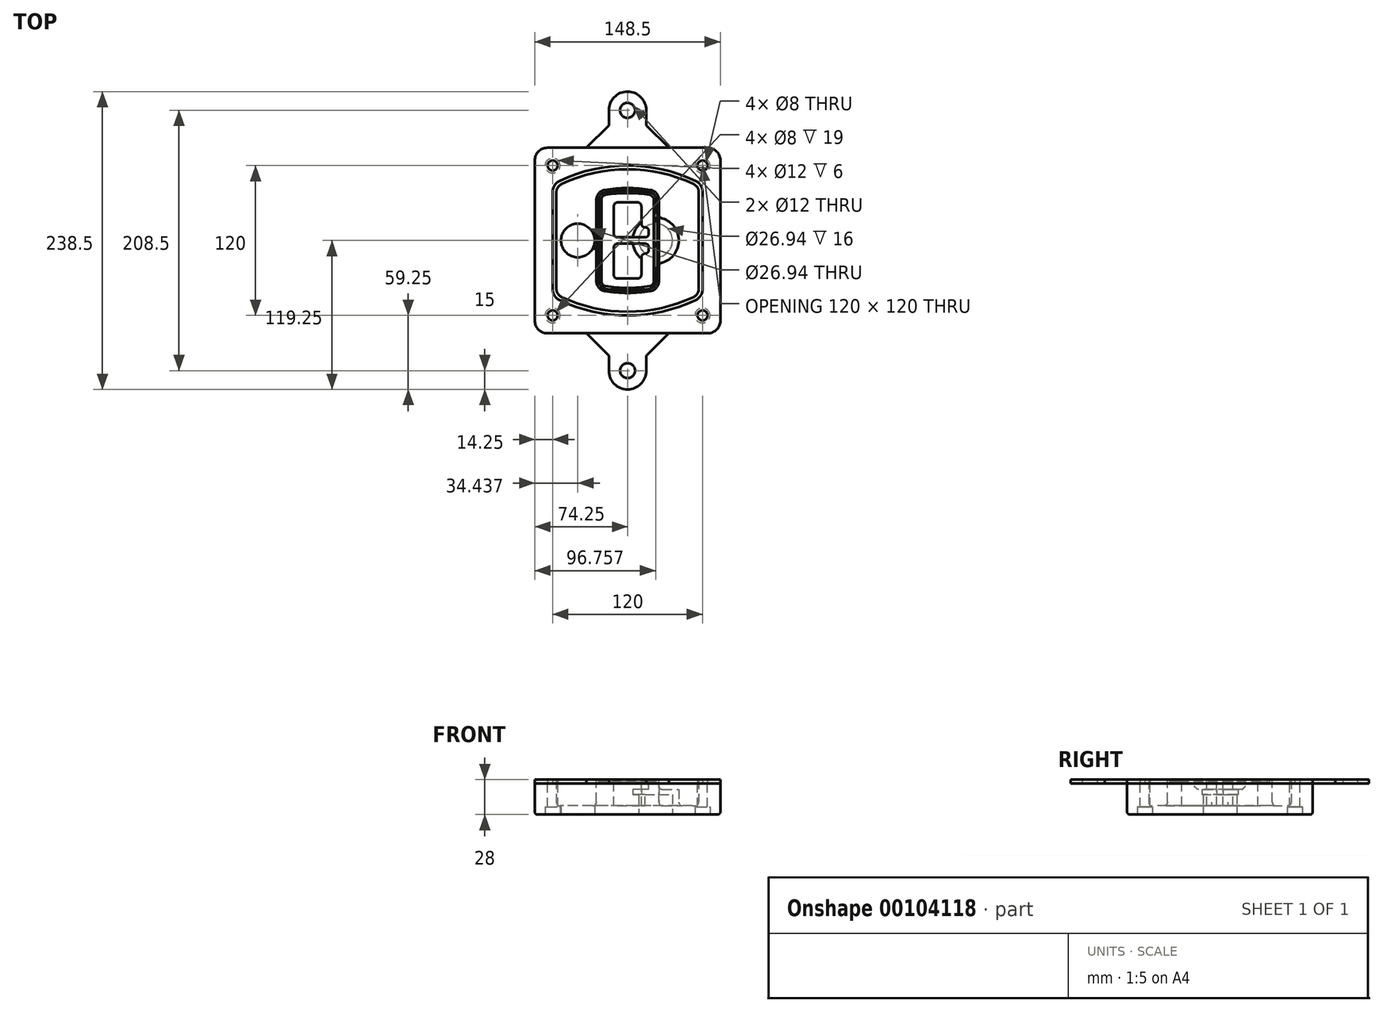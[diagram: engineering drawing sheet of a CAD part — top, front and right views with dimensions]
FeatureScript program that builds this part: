
annotation { "Feature Type Name" : "Feature", "Feature Type Description" : "" }
export const myFeature = defineFeature(function(context is Context, id is Id, definition is map)
    precondition{}
    {
        {
            var Q0;
            Q0=qCreatedBy(makeId("Top.planeOp"),FACE);
            var sketch = newSketch(context, id + "F0", { "sketchPlane" : qUnion([Q0])});
            skPoint(sketch, "E0.rect.middle", {"position": v(0, 0) * mm});
            skLineSegment(sketch, "E1.bottom", {"start": v(-64.25, -74.25) * mm, "end": v(64.25, -74.25) * mm});
            skLineSegment(sketch, "E1.top", {"start": v(-64.25, 74.25) * mm, "end": v(64.25, 74.25) * mm});
            skLineSegment(sketch, "E1.left", {"start": v(-74.25, -64.25) * mm, "end": v(-74.25, 64.25) * mm});
            skLineSegment(sketch, "E1.right", {"start": v(74.25, -64.25) * mm, "end": v(74.25, 64.25) * mm});
            skLineSegment(sketch, "E2", {"start": v(-74.25, 74.25) * mm, "end": v(74.25, -74.25) * mm, "construction": true});
            skLineSegment(sketch, "E3", {"start": v(74.25, 74.25) * mm, "end": v(-74.25, -74.25) * mm, "construction": true});
            skCircle(sketch, "E4", {"center": v(-60, 60) * mm, "radius": 4 * mm});
            skCircle(sketch, "E5", {"center": v(60, 60) * mm, "radius": 4 * mm});
            skCircle(sketch, "E6", {"center": v(60, -60) * mm, "radius": 4 * mm});
            skCircle(sketch, "E7", {"center": v(-60, -60) * mm, "radius": 4 * mm});
            skLineSegment(sketch, "E8", {"start": v(-60, 60) * mm, "end": v(60, 60) * mm, "construction": true});
            skLineSegment(sketch, "E9", {"start": v(60, 60) * mm, "end": v(60, -60) * mm, "construction": true});
            skLineSegment(sketch, "E10", {"start": v(60, -60) * mm, "end": v(-60, -60) * mm, "construction": true});
            skLineSegment(sketch, "E11", {"start": v(-60, -60) * mm, "end": v(-60, 60) * mm, "construction": true});
            skLineSegment(sketch, "E12", {"start": v(-60, 38.83) * mm, "end": v(-60, -38.83) * mm});
            skLineSegment(sketch, "E13", {"start": v(60, 38.83) * mm, "end": v(60, -38.83) * mm});
            skArc(sketch, "E14", {"start": v(54.26, 47.88) * mm, "mid": v(0, 60) * mm, "end": v(-54.26, 47.88) * mm});
            skArc(sketch, "E15", {"start": v(-54.26, -47.88) * mm, "mid": v(0, -60) * mm, "end": v(54.26, -47.88) * mm});
            skLineSegment(sketch, "E16", {"start": v(-60, 0) * mm, "end": v(60, 0) * mm, "construction": true});
            skPoint(sketch, "E17.visualSharp", {"position": v(-60, -45) * mm});
            skArc(sketch, "E17.filletArc", {"start": v(-60, -38.83) * mm, "mid": v(-58.44, -44.2) * mm, "end": v(-54.26, -47.88) * mm});
            skPoint(sketch, "E18.visualSharp", {"position": v(-60, 45) * mm});
            skArc(sketch, "E18.filletArc", {"start": v(-54.26, 47.88) * mm, "mid": v(-58.44, 44.2) * mm, "end": v(-60, 38.83) * mm});
            skPoint(sketch, "E19.visualSharp", {"position": v(60, 45) * mm});
            skArc(sketch, "E19.filletArc", {"start": v(60, 38.83) * mm, "mid": v(58.44, 44.2) * mm, "end": v(54.26, 47.88) * mm});
            skPoint(sketch, "E20.visualSharp", {"position": v(60, -45) * mm});
            skArc(sketch, "E20.filletArc", {"start": v(54.26, -47.88) * mm, "mid": v(58.44, -44.2) * mm, "end": v(60, -38.83) * mm});
            skPoint(sketch, "E21.visualSharp", {"position": v(-74.25, 74.25) * mm});
            skArc(sketch, "E21.filletArc", {"start": v(-64.25, 74.25) * mm, "mid": v(-71.32, 71.32) * mm, "end": v(-74.25, 64.25) * mm});
            skPoint(sketch, "E22.visualSharp", {"position": v(74.25, 74.25) * mm});
            skArc(sketch, "E22.filletArc", {"start": v(74.25, 64.25) * mm, "mid": v(71.32, 71.32) * mm, "end": v(64.25, 74.25) * mm});
            skPoint(sketch, "E23.visualSharp", {"position": v(74.25, -74.25) * mm});
            skArc(sketch, "E23.filletArc", {"start": v(64.25, -74.25) * mm, "mid": v(71.32, -71.32) * mm, "end": v(74.25, -64.25) * mm});
            skPoint(sketch, "E24.visualSharp", {"position": v(-74.25, -74.25) * mm});
            skArc(sketch, "E24.filletArc", {"start": v(-74.25, -64.25) * mm, "mid": v(-71.32, -71.32) * mm, "end": v(-64.25, -74.25) * mm});
            skArc(sketch, "E25.0", {"start": v(57, 38.83) * mm, "mid": v(55.9, 42.58) * mm, "end": v(52.98, 45.17) * mm});
            skLineSegment(sketch, "E25.1", {"start": v(57, 38.83) * mm, "end": v(57, -38.83) * mm});
            skArc(sketch, "E25.2", {"start": v(52.98, -45.17) * mm, "mid": v(55.9, -42.58) * mm, "end": v(57, -38.83) * mm});
            skArc(sketch, "E25.3", {"start": v(-52.98, -45.17) * mm, "mid": v(0, -57) * mm, "end": v(52.98, -45.17) * mm});
            skArc(sketch, "E25.4", {"start": v(-57, -38.83) * mm, "mid": v(-55.9, -42.58) * mm, "end": v(-52.98, -45.17) * mm});
            skArc(sketch, "E25.5", {"start": v(52.98, 45.17) * mm, "mid": v(0, 57) * mm, "end": v(-52.98, 45.17) * mm});
            skLineSegment(sketch, "E25.6", {"start": v(-57, 38.83) * mm, "end": v(-57, -38.83) * mm});
            skArc(sketch, "E25.7", {"start": v(-52.98, 45.17) * mm, "mid": v(-55.9, 42.58) * mm, "end": v(-57, 38.83) * mm});
            skArc(sketch, "E26.0", {"start": v(-55.96, 51.5) * mm, "mid": v(-61.82, 46.33) * mm, "end": v(-64, 38.83) * mm});
            skArc(sketch, "E26.1", {"start": v(55.96, 51.5) * mm, "mid": v(0, 64) * mm, "end": v(-55.96, 51.5) * mm});
            skArc(sketch, "E26.2", {"start": v(64, 38.83) * mm, "mid": v(61.82, 46.33) * mm, "end": v(55.96, 51.5) * mm});
            skLineSegment(sketch, "E26.3", {"start": v(64, 38.83) * mm, "end": v(64, -38.83) * mm});
            skArc(sketch, "E26.4", {"start": v(55.96, -51.5) * mm, "mid": v(61.82, -46.33) * mm, "end": v(64, -38.83) * mm});
            skLineSegment(sketch, "E26.5", {"start": v(-64, 38.83) * mm, "end": v(-64, -38.83) * mm});
            skArc(sketch, "E26.6", {"start": v(-55.96, -51.5) * mm, "mid": v(0, -64) * mm, "end": v(55.96, -51.5) * mm});
            skArc(sketch, "E26.7", {"start": v(-64, -38.83) * mm, "mid": v(-61.82, -46.33) * mm, "end": v(-55.96, -51.5) * mm});
            skSolve(sketch);
        }
        {
            var Q0;
            Q0=makeQuery(id+"F0.imprint","IMPRINT",FACE,{"disambiguationData":[TD([[makeQuery(id+"F0.imprint","IMPRINT",EDGE,{"derivedFrom":sQuery(id+"F0.wireOp",EDGE,"E1.bottom")}),1.0]])]});
            var Q1;
            Q1=makeQuery(id+"F0.imprint","IMPRINT",FACE,{"disambiguationData":[TD([[makeQuery(id+"F0.imprint","IMPRINT",EDGE,{"derivedFrom":sQuery(id+"F0.wireOp",EDGE,"E12")}),1.0]])]});
            var Q2;
            Q2=makeQuery(id+"F0.imprint","IMPRINT",FACE,{"disambiguationData":[TD([[makeQuery(id+"F0.imprint","IMPRINT",EDGE,{"derivedFrom":sQuery(id+"F0.wireOp",EDGE,"E25.0")}),1.0]])]});
            var Q3;
            Q3=makeQuery(id+"F0.imprint","IMPRINT",FACE,{"disambiguationData":[TD([[makeQuery(id+"F0.imprint","IMPRINT",EDGE,{"derivedFrom":sQuery(id+"F0.wireOp",EDGE,"E12")}),-1.0]])]});
            extrude(context, id + "F1", {"entities" : qUnion([Q0, Q1, Q2, Q3]), "oppositeDirection" : true, "depth" : 25 * mm});
        }
        {
            var Q0;
            Q0=makeQuery(id+"F0.imprint","IMPRINT",FACE,{"disambiguationData":[TD([[makeQuery(id+"F0.imprint","IMPRINT",EDGE,{"derivedFrom":sQuery(id+"F0.wireOp",EDGE,"E12")}),1.0]])]});
            extrude(context, id + "F2", {"entities" : qUnion([Q0]), "operationType" : NewBodyOperationType.ADD, "depth" : 3 * mm});
        }
        {
            var Q0;
            Q0=makeQuery(id+"F0.imprint","IMPRINT",FACE,{"disambiguationData":[TD([[makeQuery(id+"F0.imprint","IMPRINT",EDGE,{"derivedFrom":sQuery(id+"F0.wireOp",EDGE,"E25.0")}),1.0]])]});
            extrude(context, id + "F3", {"entities" : qUnion([Q0]), "operationType" : NewBodyOperationType.REMOVE, "oppositeDirection" : true, "depth" : 18 * mm});
        }
        {
            var Q0;
            Q0=makeQuery(id+"F2.opExtrude","CAP_FACE",FACE,{"disambiguationData":[OSD([sQuery(id+"F0.wireOp",EDGE,"E12"),sQuery(id+"F0.wireOp",EDGE,"E13"),sQuery(id+"F0.wireOp",EDGE,"E14"),sQuery(id+"F0.wireOp",EDGE,"E15"),sQuery(id+"F0.wireOp",EDGE,"E17.filletArc"),sQuery(id+"F0.wireOp",EDGE,"E18.filletArc"),sQuery(id+"F0.wireOp",EDGE,"E19.filletArc"),sQuery(id+"F0.wireOp",EDGE,"E20.filletArc"),sQuery(id+"F0.wireOp",EDGE,"E25.0"),sQuery(id+"F0.wireOp",EDGE,"E25.1"),sQuery(id+"F0.wireOp",EDGE,"E25.2"),sQuery(id+"F0.wireOp",EDGE,"E25.3"),sQuery(id+"F0.wireOp",EDGE,"E25.4"),sQuery(id+"F0.wireOp",EDGE,"E25.5"),sQuery(id+"F0.wireOp",EDGE,"E25.6"),sQuery(id+"F0.wireOp",EDGE,"E25.7")])],"isStart":false});
            var sketch = newSketch(context, id + "F4", { "sketchPlane" : qUnion([Q0])});
            skArc(sketch, "E27.0", {"start": v(-18.34, -40.45) * mm, "mid": v(0, -42) * mm, "end": v(18.34, -40.45) * mm});
            skArc(sketch, "E28.0", {"start": v(18.34, 40.45) * mm, "mid": v(0, 42) * mm, "end": v(-18.34, 40.45) * mm});
            skLineSegment(sketch, "E29", {"start": v(-25, 32.57) * mm, "end": v(-25, -32.57) * mm});
            skLineSegment(sketch, "E30", {"start": v(25, 32.57) * mm, "end": v(25, -32.57) * mm});
            skLineSegment(sketch, "E31", {"start": v(-25, 39.1) * mm, "end": v(25, 39.1) * mm, "construction": true});
            skLineSegment(sketch, "E32", {"start": v(-25, -39.1) * mm, "end": v(25, -39.1) * mm, "construction": true});
            skPoint(sketch, "E33.visualSharp", {"position": v(-25, 39.1) * mm});
            skArc(sketch, "E33.filletArc", {"start": v(-18.34, 40.45) * mm, "mid": v(-23.11, 37.73) * mm, "end": v(-25, 32.57) * mm});
            skPoint(sketch, "E34.visualSharp", {"position": v(25, 39.1) * mm});
            skArc(sketch, "E34.filletArc", {"start": v(25, 32.57) * mm, "mid": v(23.11, 37.73) * mm, "end": v(18.34, 40.45) * mm});
            skPoint(sketch, "E35.visualSharp", {"position": v(25, -39.1) * mm});
            skArc(sketch, "E35.filletArc", {"start": v(18.34, -40.45) * mm, "mid": v(23.11, -37.73) * mm, "end": v(25, -32.57) * mm});
            skPoint(sketch, "E36.visualSharp", {"position": v(-25, -39.1) * mm});
            skArc(sketch, "E36.filletArc", {"start": v(-25, -32.57) * mm, "mid": v(-23.11, -37.73) * mm, "end": v(-18.34, -40.45) * mm});
            skArc(sketch, "E37.0", {"start": v(52.98, 45.17) * mm, "mid": v(0, 57) * mm, "end": v(-52.98, 45.17) * mm});
            skArc(sketch, "E37.1", {"start": v(-52.98, 45.17) * mm, "mid": v(-55.9, 42.58) * mm, "end": v(-57, 38.83) * mm});
            skLineSegment(sketch, "E37.2", {"start": v(-57, 38.83) * mm, "end": v(-57, -38.83) * mm});
            skArc(sketch, "E37.3", {"start": v(-57, -38.83) * mm, "mid": v(-55.9, -42.58) * mm, "end": v(-52.98, -45.17) * mm});
            skArc(sketch, "E37.4", {"start": v(-52.98, -45.17) * mm, "mid": v(0, -57) * mm, "end": v(52.98, -45.17) * mm});
            skArc(sketch, "E37.5", {"start": v(52.98, -45.17) * mm, "mid": v(55.9, -42.58) * mm, "end": v(57, -38.83) * mm});
            skLineSegment(sketch, "E37.6", {"start": v(57, 38.83) * mm, "end": v(57, -38.83) * mm});
            skArc(sketch, "E37.7", {"start": v(57, 38.83) * mm, "mid": v(55.9, 42.58) * mm, "end": v(52.98, 45.17) * mm});
            skLineSegment(sketch, "E38.0", {"start": v(23, 32.57) * mm, "end": v(23, -32.57) * mm});
            skArc(sketch, "E38.1", {"start": v(18, -38.48) * mm, "mid": v(21.58, -36.44) * mm, "end": v(23, -32.57) * mm});
            skArc(sketch, "E38.2", {"start": v(-18, -38.48) * mm, "mid": v(0, -40) * mm, "end": v(18, -38.48) * mm});
            skArc(sketch, "E38.3", {"start": v(-23, -32.57) * mm, "mid": v(-21.58, -36.44) * mm, "end": v(-18, -38.48) * mm});
            skLineSegment(sketch, "E38.4", {"start": v(-23, 32.57) * mm, "end": v(-23, -32.57) * mm});
            skArc(sketch, "E38.5", {"start": v(23, 32.57) * mm, "mid": v(21.58, 36.44) * mm, "end": v(18, 38.48) * mm});
            skArc(sketch, "E38.6", {"start": v(-18, 38.48) * mm, "mid": v(-21.58, 36.44) * mm, "end": v(-23, 32.57) * mm});
            skArc(sketch, "E38.7", {"start": v(18, 38.48) * mm, "mid": v(0, 40) * mm, "end": v(-18, 38.48) * mm});
            skArc(sketch, "E39.0", {"start": v(21, 32.57) * mm, "mid": v(20.06, 35.15) * mm, "end": v(17.67, 36.5) * mm});
            skLineSegment(sketch, "E39.1", {"start": v(21, 32.57) * mm, "end": v(21, -32.57) * mm});
            skArc(sketch, "E39.2", {"start": v(17.67, -36.5) * mm, "mid": v(20.06, -35.15) * mm, "end": v(21, -32.57) * mm});
            skArc(sketch, "E39.3", {"start": v(-17.67, -36.5) * mm, "mid": v(0, -38) * mm, "end": v(17.67, -36.5) * mm});
            skArc(sketch, "E39.4", {"start": v(-21, -32.57) * mm, "mid": v(-20.06, -35.15) * mm, "end": v(-17.67, -36.5) * mm});
            skArc(sketch, "E39.5", {"start": v(17.67, 36.5) * mm, "mid": v(0, 38) * mm, "end": v(-17.67, 36.5) * mm});
            skLineSegment(sketch, "E39.6", {"start": v(-21, 32.57) * mm, "end": v(-21, -32.57) * mm});
            skArc(sketch, "E39.7", {"start": v(-17.67, 36.5) * mm, "mid": v(-20.06, 35.15) * mm, "end": v(-21, 32.57) * mm});
            skLineSegment(sketch, "E40", {"start": v(-25, 0) * mm, "end": v(25, 0) * mm, "construction": true});
            skLineSegment(sketch, "E41", {"start": v(-11, 5.5) * mm, "end": v(-11, 27.5) * mm});
            skLineSegment(sketch, "E42", {"start": v(-8, 30.5) * mm, "end": v(8, 30.5) * mm});
            skLineSegment(sketch, "E43", {"start": v(11, 27.5) * mm, "end": v(11, 13.5) * mm});
            skLineSegment(sketch, "E44", {"start": v(14, 10.5) * mm, "end": v(14, 10.5) * mm});
            skLineSegment(sketch, "E45", {"start": v(17, 7.5) * mm, "end": v(17, 5.5) * mm});
            skLineSegment(sketch, "E46", {"start": v(14, 2.5) * mm, "end": v(-8, 2.5) * mm});
            skPoint(sketch, "E47.visualSharp", {"position": v(-11, 30.5) * mm});
            skArc(sketch, "E47.filletArc", {"start": v(-8, 30.5) * mm, "mid": v(-10.12, 29.62) * mm, "end": v(-11, 27.5) * mm});
            skPoint(sketch, "E48.visualSharp", {"position": v(11, 30.5) * mm});
            skArc(sketch, "E48.filletArc", {"start": v(11, 27.5) * mm, "mid": v(10.12, 29.62) * mm, "end": v(8, 30.5) * mm});
            skPoint(sketch, "E49.visualSharp", {"position": v(11, 10.5) * mm});
            skArc(sketch, "E49.filletArc", {"start": v(11, 13.5) * mm, "mid": v(11.88, 11.38) * mm, "end": v(14, 10.5) * mm});
            skPoint(sketch, "E50.visualSharp", {"position": v(17, 10.5) * mm});
            skArc(sketch, "E50.filletArc", {"start": v(17, 7.5) * mm, "mid": v(16.12, 9.62) * mm, "end": v(14, 10.5) * mm});
            skPoint(sketch, "E51.visualSharp", {"position": v(17, 2.5) * mm});
            skArc(sketch, "E51.filletArc", {"start": v(14, 2.5) * mm, "mid": v(16.12, 3.38) * mm, "end": v(17, 5.5) * mm});
            skPoint(sketch, "E52.visualSharp", {"position": v(-11, 2.5) * mm});
            skArc(sketch, "E52.filletArc", {"start": v(-11, 5.5) * mm, "mid": v(-10.12, 3.38) * mm, "end": v(-8, 2.5) * mm});
            skLineSegment(sketch, "E53.0.MirrorCS", {"start": v(14, -2.5) * mm, "end": v(-8, -2.5) * mm});
            skArc(sketch, "E54.0.MirrorCS", {"start": v(-11, -5.5) * mm, "mid": v(-10.12, -3.38) * mm, "end": v(-8, -2.5) * mm});
            skLineSegment(sketch, "E55.0.MirrorCS", {"start": v(-11, -5.5) * mm, "end": v(-11, -27.5) * mm});
            skArc(sketch, "E56.0.MirrorCS", {"start": v(-8, -30.5) * mm, "mid": v(-10.12, -29.62) * mm, "end": v(-11, -27.5) * mm});
            skLineSegment(sketch, "E57.0.MirrorCS", {"start": v(-8, -30.5) * mm, "end": v(8, -30.5) * mm});
            skArc(sketch, "E58.0.MirrorCS", {"start": v(11, -27.5) * mm, "mid": v(10.12, -29.62) * mm, "end": v(8, -30.5) * mm});
            skLineSegment(sketch, "E59.0.MirrorCS", {"start": v(11, -27.5) * mm, "end": v(11, -13.5) * mm});
            skArc(sketch, "E60.0.MirrorCS", {"start": v(11, -13.5) * mm, "mid": v(11.88, -11.38) * mm, "end": v(14, -10.5) * mm});
            skArc(sketch, "E61.0.MirrorCS", {"start": v(17, -7.5) * mm, "mid": v(16.12, -9.62) * mm, "end": v(14, -10.5) * mm});
            skLineSegment(sketch, "E62.0.MirrorCS", {"start": v(17, -7.5) * mm, "end": v(17, -5.5) * mm});
            skArc(sketch, "E63.0.MirrorCS", {"start": v(14, -2.5) * mm, "mid": v(16.12, -3.38) * mm, "end": v(17, -5.5) * mm});
            skSolve(sketch);
        }
        {
            var Q0;
            Q0=makeQuery(id+"F4.imprint","IMPRINT",FACE,{"disambiguationData":[TD([[makeQuery(id+"F4.imprint","IMPRINT",EDGE,{"derivedFrom":sQuery(id+"F4.wireOp",EDGE,"E27.0")}),1.0]])]});
            var Q1;
            Q1=makeQuery(id+"F4.imprint","IMPRINT",FACE,{"disambiguationData":[TD([[makeQuery(id+"F4.imprint","IMPRINT",EDGE,{"derivedFrom":sQuery(id+"F4.wireOp",EDGE,"E38.0")}),-1.0]])]});
            var Q2;
            Q2=makeQuery(id+"F4.imprint","IMPRINT",FACE,{"disambiguationData":[TD([[makeQuery(id+"F4.imprint","IMPRINT",EDGE,{"derivedFrom":sQuery(id+"F4.wireOp",EDGE,"E39.0")}),1.0]])]});
            extrude(context, id + "F5", {"entities" : qUnion([Q0, Q1, Q2]), "operationType" : NewBodyOperationType.ADD, "endBound" : BoundingType.UP_TO_NEXT, "oppositeDirection" : true, "depth" : 25 * mm});
        }
        {
            var Q0;
            Q0=makeQuery(id+"F4.imprint","IMPRINT",FACE,{"disambiguationData":[TD([[makeQuery(id+"F4.imprint","IMPRINT",EDGE,{"derivedFrom":sQuery(id+"F4.wireOp",EDGE,"E38.0")}),-1.0]])]});
            extrude(context, id + "F6", {"entities" : qUnion([Q0]), "operationType" : NewBodyOperationType.REMOVE, "oppositeDirection" : true, "depth" : 2 * mm});
        }
        {
            var Q0;
            Q0=makeQuery(id+"F1.opExtrude","CAP_FACE",FACE,{"disambiguationData":[OSD([sQuery(id+"F0.wireOp",EDGE,"E1.bottom"),sQuery(id+"F0.wireOp",EDGE,"E1.top"),sQuery(id+"F0.wireOp",EDGE,"E1.left"),sQuery(id+"F0.wireOp",EDGE,"E1.right"),sQuery(id+"F0.wireOp",EDGE,"E4"),sQuery(id+"F0.wireOp",EDGE,"E5"),sQuery(id+"F0.wireOp",EDGE,"E6"),sQuery(id+"F0.wireOp",EDGE,"E7"),sQuery(id+"F0.wireOp",EDGE,"E21.filletArc"),sQuery(id+"F0.wireOp",EDGE,"E22.filletArc"),sQuery(id+"F0.wireOp",EDGE,"E23.filletArc"),sQuery(id+"F0.wireOp",EDGE,"E24.filletArc")])],"isStart":false});
            var sketch = newSketch(context, id + "F7", { "sketchPlane" : qUnion([Q0])});
            skCircle(sketch, "E64", {"center": v(22.5, 0) * mm, "radius": 13.47 * mm});
            skCircle(sketch, "E65", {"center": v(-39.81, 0) * mm, "radius": 13.47 * mm});
            skLineSegment(sketch, "E66", {"start": v(74.25, 0) * mm, "end": v(-74.25, 0) * mm});
            skCircle(sketch, "E67", {"center": v(22.5, 0) * mm, "radius": 18.47 * mm});
            skCircle(sketch, "E68", {"center": v(60, -60) * mm, "radius": 6 * mm});
            skCircle(sketch, "E69", {"center": v(-60, -60) * mm, "radius": 6 * mm});
            skCircle(sketch, "E70", {"center": v(-60, 60) * mm, "radius": 6 * mm});
            skCircle(sketch, "E71", {"center": v(60, 60) * mm, "radius": 6 * mm});
            skSolve(sketch);
        }
        {
            var Q0;
            {var subQ1=sQuery(id+"F7.wireOp",EDGE,"E66");var subQ4=sQuery(id+"F7.wireOp",EDGE,"E64");var subQ6=makeQuery(id+"F7.imprint","INTERSECT",VERTEX,{"disambiguationData":[OD(0.0)],"derivedFrom":[subQ4,subQ1]});Q0=makeQuery(id+"F7.imprint","IMPRINT",FACE,{"disambiguationData":[TD([[makeQuery(id+"F7.imprint","IMPRINT",EDGE,{"disambiguationData":[TD([[subQ6,-1.0]])],"derivedFrom":subQ4}),-1.0]])]});}
            var Q1;
            {var subQ0=sQuery(id+"F7.wireOp",EDGE,"E66");var subQ1=sQuery(id+"F7.wireOp",EDGE,"E64");var subQ3=makeQuery(id+"F7.imprint","INTERSECT",VERTEX,{"disambiguationData":[OD(0.0)],"derivedFrom":[subQ1,subQ0]});Q1=makeQuery(id+"F7.imprint","IMPRINT",FACE,{"disambiguationData":[TD([[makeQuery(id+"F7.imprint","IMPRINT",EDGE,{"disambiguationData":[TD([[subQ3,-1.0]])],"derivedFrom":subQ1}),1.0]])]});}
            var Q2;
            {var subQ0=sQuery(id+"F7.wireOp",EDGE,"E66");var subQ1=sQuery(id+"F7.wireOp",EDGE,"E64");var subQ3=makeQuery(id+"F7.imprint","INTERSECT",VERTEX,{"disambiguationData":[OD(0.0)],"derivedFrom":[subQ1,subQ0]});Q2=makeQuery(id+"F7.imprint","IMPRINT",FACE,{"disambiguationData":[TD([[makeQuery(id+"F7.imprint","IMPRINT",EDGE,{"disambiguationData":[TD([[subQ3,1.0]])],"derivedFrom":subQ1}),1.0]])]});}
            var Q3;
            {var subQ1=sQuery(id+"F7.wireOp",EDGE,"E66");var subQ4=sQuery(id+"F7.wireOp",EDGE,"E64");var subQ6=makeQuery(id+"F7.imprint","INTERSECT",VERTEX,{"disambiguationData":[OD(0.0)],"derivedFrom":[subQ4,subQ1]});Q3=makeQuery(id+"F7.imprint","IMPRINT",FACE,{"disambiguationData":[TD([[makeQuery(id+"F7.imprint","IMPRINT",EDGE,{"disambiguationData":[TD([[subQ6,1.0]])],"derivedFrom":subQ4}),-1.0]])]});}
            extrude(context, id + "F8", {"entities" : qUnion([Q0, Q1, Q2, Q3]), "operationType" : NewBodyOperationType.ADD, "oppositeDirection" : true, "depth" : 20 * mm});
        }
        {
            var Q0;
            {var subQ0=sQuery(id+"F7.wireOp",EDGE,"E66");var subQ1=sQuery(id+"F7.wireOp",EDGE,"E64");var subQ3=makeQuery(id+"F7.imprint","INTERSECT",VERTEX,{"disambiguationData":[OD(0.0)],"derivedFrom":[subQ1,subQ0]});Q0=makeQuery(id+"F7.imprint","IMPRINT",FACE,{"disambiguationData":[TD([[makeQuery(id+"F7.imprint","IMPRINT",EDGE,{"disambiguationData":[TD([[subQ3,-1.0]])],"derivedFrom":subQ1}),1.0]])]});}
            var Q1;
            {var subQ0=sQuery(id+"F7.wireOp",EDGE,"E66");var subQ1=sQuery(id+"F7.wireOp",EDGE,"E64");var subQ3=makeQuery(id+"F7.imprint","INTERSECT",VERTEX,{"disambiguationData":[OD(0.0)],"derivedFrom":[subQ1,subQ0]});Q1=makeQuery(id+"F7.imprint","IMPRINT",FACE,{"disambiguationData":[TD([[makeQuery(id+"F7.imprint","IMPRINT",EDGE,{"disambiguationData":[TD([[subQ3,1.0]])],"derivedFrom":subQ1}),1.0]])]});}
            extrude(context, id + "F9", {"entities" : qUnion([Q0, Q1]), "operationType" : NewBodyOperationType.REMOVE, "oppositeDirection" : true, "depth" : 16 * mm});
        }
        {
            var Q0;
            {var subQ0=sQuery(id+"F7.wireOp",EDGE,"E66");var subQ1=sQuery(id+"F7.wireOp",EDGE,"E65");var subQ3=makeQuery(id+"F7.imprint","INTERSECT",VERTEX,{"disambiguationData":[OD(0.0)],"derivedFrom":[subQ1,subQ0]});Q0=makeQuery(id+"F7.imprint","IMPRINT",FACE,{"disambiguationData":[TD([[makeQuery(id+"F7.imprint","IMPRINT",EDGE,{"disambiguationData":[TD([[subQ3,-1.0]])],"derivedFrom":subQ1}),1.0]])]});}
            var Q1;
            {var subQ0=sQuery(id+"F7.wireOp",EDGE,"E66");var subQ1=sQuery(id+"F7.wireOp",EDGE,"E65");var subQ3=makeQuery(id+"F7.imprint","INTERSECT",VERTEX,{"disambiguationData":[OD(0.0)],"derivedFrom":[subQ1,subQ0]});Q1=makeQuery(id+"F7.imprint","IMPRINT",FACE,{"disambiguationData":[TD([[makeQuery(id+"F7.imprint","IMPRINT",EDGE,{"disambiguationData":[TD([[subQ3,1.0]])],"derivedFrom":subQ1}),1.0]])]});}
            extrude(context, id + "F10", {"entities" : qUnion([Q0, Q1]), "operationType" : NewBodyOperationType.REMOVE, "oppositeDirection" : true, "depth" : 25 * mm});
        }
        {
            var Q0;
            Q0=makeQuery(id+"F7.imprint","IMPRINT",FACE,{"disambiguationData":[TD([[makeQuery(id+"F7.imprint","IMPRINT",EDGE,{"derivedFrom":sQuery(id+"F7.wireOp",EDGE,"E68")}),1.0]])]});
            var Q1;
            Q1=makeQuery(id+"F7.imprint","IMPRINT",FACE,{"disambiguationData":[TD([[makeQuery(id+"F7.imprint","IMPRINT",EDGE,{"derivedFrom":makeQuery(id+"F1.opExtrude","CAP_EDGE",EDGE,{"disambiguationData":[OSD([sQuery(id+"F0.wireOp",EDGE,"E5")])],"isStart":false})}),-1.0]])]});
            var Q2;
            Q2=makeQuery(id+"F7.imprint","IMPRINT",FACE,{"disambiguationData":[TD([[makeQuery(id+"F7.imprint","IMPRINT",EDGE,{"derivedFrom":sQuery(id+"F7.wireOp",EDGE,"E69")}),1.0]])]});
            var Q3;
            Q3=makeQuery(id+"F7.imprint","IMPRINT",FACE,{"disambiguationData":[TD([[makeQuery(id+"F7.imprint","IMPRINT",EDGE,{"derivedFrom":makeQuery(id+"F1.opExtrude","CAP_EDGE",EDGE,{"disambiguationData":[OSD([sQuery(id+"F0.wireOp",EDGE,"E4")])],"isStart":false})}),-1.0]])]});
            var Q4;
            Q4=makeQuery(id+"F7.imprint","IMPRINT",FACE,{"disambiguationData":[TD([[makeQuery(id+"F7.imprint","IMPRINT",EDGE,{"derivedFrom":sQuery(id+"F7.wireOp",EDGE,"E70")}),1.0]])]});
            var Q5;
            Q5=makeQuery(id+"F7.imprint","IMPRINT",FACE,{"disambiguationData":[TD([[makeQuery(id+"F7.imprint","IMPRINT",EDGE,{"derivedFrom":makeQuery(id+"F1.opExtrude","CAP_EDGE",EDGE,{"disambiguationData":[OSD([sQuery(id+"F0.wireOp",EDGE,"E7")])],"isStart":false})}),-1.0]])]});
            var Q6;
            Q6=makeQuery(id+"F7.imprint","IMPRINT",FACE,{"disambiguationData":[TD([[makeQuery(id+"F7.imprint","IMPRINT",EDGE,{"derivedFrom":sQuery(id+"F7.wireOp",EDGE,"E71")}),1.0]])]});
            var Q7;
            Q7=makeQuery(id+"F7.imprint","IMPRINT",FACE,{"disambiguationData":[TD([[makeQuery(id+"F7.imprint","IMPRINT",EDGE,{"derivedFrom":makeQuery(id+"F1.opExtrude","CAP_EDGE",EDGE,{"disambiguationData":[OSD([sQuery(id+"F0.wireOp",EDGE,"E6")])],"isStart":false})}),-1.0]])]});
            extrude(context, id + "F11", {"entities" : qUnion([Q0, Q1, Q2, Q3, Q4, Q5, Q6, Q7]), "operationType" : NewBodyOperationType.REMOVE, "oppositeDirection" : true, "depth" : 6 * mm});
        }
        {
            var Q0;
            Q0=makeQuery(id+"F9.boolean.opBoolean","COPY",FACE,{"derivedFrom":makeQuery(id+"F9.opExtrude","CAP_FACE",FACE,{"disambiguationData":[OSD([sQuery(id+"F7.wireOp",EDGE,"E64")])],"isStart":false})});
            var sketch = newSketch(context, id + "F12", { "sketchPlane" : qUnion([Q0])});
            skArc(sketch, "E72.0", {"start": v(11, 14.45) * mm, "mid": v(6.45, 9.13) * mm, "end": v(4.2, 2.5) * mm});
            skArc(sketch, "E72.1", {"start": v(4.2, -2.5) * mm, "mid": v(6.45, -9.13) * mm, "end": v(11, -14.45) * mm});
            skLineSegment(sketch, "E73", {"start": v(4.2, -2.5) * mm, "end": v(14, -2.5) * mm});
            skLineSegment(sketch, "E74.0", {"start": v(14, 2.5) * mm, "end": v(4.2, 2.5) * mm});
            skArc(sketch, "E74.1", {"start": v(14, 2.5) * mm, "mid": v(16.12, 3.38) * mm, "end": v(17, 5.5) * mm});
            skLineSegment(sketch, "E74.2", {"start": v(17, 7.5) * mm, "end": v(17, 5.5) * mm});
            skArc(sketch, "E74.3", {"start": v(17, 7.5) * mm, "mid": v(16.12, 9.62) * mm, "end": v(14, 10.5) * mm});
            skArc(sketch, "E74.4", {"start": v(11, 13.5) * mm, "mid": v(11.88, 11.38) * mm, "end": v(14, 10.5) * mm});
            skLineSegment(sketch, "E74.5", {"start": v(11, 14.45) * mm, "end": v(11, 13.5) * mm});
            skLineSegment(sketch, "E74.7", {"start": v(14, -2.5) * mm, "end": v(4.2, -2.5) * mm});
            skArc(sketch, "E74.8", {"start": v(14, -2.5) * mm, "mid": v(16.12, -3.38) * mm, "end": v(17, -5.5) * mm});
            skLineSegment(sketch, "E74.9", {"start": v(17, -7.5) * mm, "end": v(17, -5.5) * mm});
            skArc(sketch, "E74.10", {"start": v(17, -7.5) * mm, "mid": v(16.12, -9.62) * mm, "end": v(14, -10.5) * mm});
            skArc(sketch, "E74.11", {"start": v(11, -13.5) * mm, "mid": v(11.88, -11.38) * mm, "end": v(14, -10.5) * mm});
            skLineSegment(sketch, "E74.12", {"start": v(11, -14.45) * mm, "end": v(11, -13.5) * mm});
            skPoint(sketch, "E75.orphan", {"position": v(11, -27.5) * mm});
            skPoint(sketch, "E76.orphan", {"position": v(-8, -2.5) * mm});
            skPoint(sketch, "E77.orphan", {"position": v(-8, 2.5) * mm});
            skPoint(sketch, "E78.orphan", {"position": v(11, 27.5) * mm});
            skSolve(sketch);
        }
        {
            var Q0;
            {var subQ7=sQuery(id+"F12.wireOp",EDGE,"E72.0");var subQ14=sQuery(id+"F12.wireOp",EDGE,"E72.1");var subQ16=sQuery(id+"F12.wireOp",EDGE,"E74.1");var subQ18=sQuery(id+"F12.wireOp",EDGE,"E74.8");Q0=qUnion([makeQuery(id+"F12.imprint","IMPRINT",FACE,{"disambiguationData":[TD([[makeQuery(id+"F12.imprint","IMPRINT",EDGE,{"derivedFrom":subQ7}),1.0]])]}),makeQuery(id+"F12.imprint","IMPRINT",FACE,{"disambiguationData":[TD([[makeQuery(id+"F12.imprint","IMPRINT",EDGE,{"derivedFrom":subQ14}),1.0]])]}),makeQuery(id+"F12.imprint","IMPRINT",FACE,{"disambiguationData":[TD([[makeQuery(id+"F12.imprint","IMPRINT",EDGE,{"derivedFrom":subQ16}),1.0]])]}),makeQuery(id+"F12.imprint","IMPRINT",FACE,{"disambiguationData":[TD([[makeQuery(id+"F12.imprint","IMPRINT",EDGE,{"derivedFrom":subQ18}),-1.0]])]})]);}
            var Q1;
            Q1=makeQuery(id+"F5.boolean.opBoolean","SPLIT",FACE,{"disambiguationData":[TD([makeQuery(id+"F5.opExtrude","SWEPT_FACE",FACE,{"disambiguationData":[OSD([sQuery(id+"F4.wireOp",EDGE,"E41")])]})])],"derivedFrom":makeQuery(id+"F3.boolean.opBoolean","COPY",FACE,{"derivedFrom":makeQuery(id+"F3.opExtrude","CAP_FACE",FACE,{"disambiguationData":[OSD([sQuery(id+"F0.wireOp",EDGE,"E25.0"),sQuery(id+"F0.wireOp",EDGE,"E25.1"),sQuery(id+"F0.wireOp",EDGE,"E25.2"),sQuery(id+"F0.wireOp",EDGE,"E25.3"),sQuery(id+"F0.wireOp",EDGE,"E25.4"),sQuery(id+"F0.wireOp",EDGE,"E25.5"),sQuery(id+"F0.wireOp",EDGE,"E25.6"),sQuery(id+"F0.wireOp",EDGE,"E25.7")])],"isStart":false})})});
            extrude(context, id + "F13", {"entities" : qUnion([Q0]), "operationType" : NewBodyOperationType.REMOVE, "endBound" : BoundingType.UP_TO_SURFACE, "endBoundEntityFace" : qUnion([Q1]), "depth" : 25 * mm});
        }
        {
            var Q0;
            Q0=makeQuery(id+"F3.boolean.opBoolean","COPY",EDGE,{"derivedFrom":makeQuery(id+"F3.opExtrude","CAP_EDGE",EDGE,{"disambiguationData":[OSD([sQuery(id+"F0.wireOp",EDGE,"E25.6")])],"isStart":false})});
            var Q1;
            Q1=makeQuery(id+"F8.boolean.opBoolean","INTERSECT",EDGE,{"derivedFrom":[makeQuery(id+"F5.opExtrude","SWEPT_FACE",FACE,{"disambiguationData":[OSD([sQuery(id+"F4.wireOp",EDGE,"E30")])]}),makeQuery(id+"F8.opExtrude","CAP_FACE",FACE,{"disambiguationData":[OSD([sQuery(id+"F7.wireOp",EDGE,"E67")])],"isStart":false})]});
            var Q2;
            Q2=makeQuery(id+"F8.boolean.opBoolean","INTERSECT",EDGE,{"disambiguationData":[OD(1.0)],"derivedFrom":[makeQuery(id+"F5.opExtrude","SWEPT_FACE",FACE,{"disambiguationData":[OSD([sQuery(id+"F4.wireOp",EDGE,"E30")])]}),makeQuery(id+"F8.opExtrude","SWEPT_FACE",FACE,{"disambiguationData":[OSD([sQuery(id+"F7.wireOp",EDGE,"E67")])]})]});
            var Q3;
            {var subQ0=sQuery(id+"F4.wireOp",EDGE,"E30");Q3=makeQuery(id+"F8.boolean.opBoolean","SPLIT",EDGE,{"disambiguationData":[TD([makeQuery(id+"F5.opExtrude","SWEPT_FACE",FACE,{"disambiguationData":[OSD([sQuery(id+"F4.wireOp",EDGE,"E35.filletArc")])]})])],"derivedFrom":makeQuery(id+"F5.opExtrude","CAP_EDGE",EDGE,{"disambiguationData":[OSD([subQ0])],"isStart":false})});}
            var Q4;
            {var subQ0=sQuery(id+"F0.wireOp",EDGE,"E25.7");var subQ1=sQuery(id+"F0.wireOp",EDGE,"E25.1");var subQ2=sQuery(id+"F0.wireOp",EDGE,"E25.6");var subQ3=sQuery(id+"F0.wireOp",EDGE,"E25.5");var subQ4=sQuery(id+"F0.wireOp",EDGE,"E25.4");var subQ5=sQuery(id+"F0.wireOp",EDGE,"E25.0");var subQ6=sQuery(id+"F0.wireOp",EDGE,"E25.2");var subQ7=sQuery(id+"F0.wireOp",EDGE,"E25.3");Q4=makeQuery(id+"F8.boolean.opBoolean","INTERSECT",EDGE,{"derivedFrom":[makeQuery(id+"F5.boolean.opBoolean","SPLIT",FACE,{"disambiguationData":[TD([makeQuery(id+"F2.opExtrude","SWEPT_FACE",FACE,{"disambiguationData":[OSD([subQ5])]})])],"derivedFrom":makeQuery(id+"F3.boolean.opBoolean","COPY",FACE,{"derivedFrom":makeQuery(id+"F3.opExtrude","CAP_FACE",FACE,{"disambiguationData":[OSD([subQ5,subQ1,subQ6,subQ7,subQ4,subQ3,subQ2,subQ0])],"isStart":false})})}),makeQuery(id+"F8.opExtrude","SWEPT_FACE",FACE,{"disambiguationData":[OSD([sQuery(id+"F7.wireOp",EDGE,"E67")])]})]});}
            var Q5;
            Q5=makeQuery(id+"F8.boolean.opBoolean","INTERSECT",EDGE,{"disambiguationData":[OD(0.0)],"derivedFrom":[makeQuery(id+"F5.opExtrude","SWEPT_FACE",FACE,{"disambiguationData":[OSD([sQuery(id+"F4.wireOp",EDGE,"E30")])]}),makeQuery(id+"F8.opExtrude","SWEPT_FACE",FACE,{"disambiguationData":[OSD([sQuery(id+"F7.wireOp",EDGE,"E67")])]})]});
            fillet(context, id + "F14", {"entities" : qUnion([Q0, Q1, Q2, Q3, Q4, Q5]), "radius" : 3 * mm, "tangentPropagation" : true, "allowEdgeOverflow" : false});
        }
        {
            var Q0;
            Q0=makeQuery(id+"F1.opExtrude","CAP_EDGE",EDGE,{"disambiguationData":[OSD([sQuery(id+"F0.wireOp",EDGE,"E1.bottom")])],"isStart":false});
            fillet(context, id + "F15", {"entities" : qUnion([Q0]), "radius" : 2 * mm, "tangentPropagation" : true, "allowEdgeOverflow" : false});
        }
        {
            var Q0;
            {var subQ0=sQuery(id+"F0.wireOp",EDGE,"E22.filletArc");var subQ1=sQuery(id+"F0.wireOp",EDGE,"E7");var subQ2=sQuery(id+"F0.wireOp",EDGE,"E6");var subQ3=sQuery(id+"F0.wireOp",EDGE,"E5");var subQ4=sQuery(id+"F0.wireOp",EDGE,"E4");var subQ5=sQuery(id+"F0.wireOp",EDGE,"E1.bottom");var subQ6=sQuery(id+"F0.wireOp",EDGE,"E21.filletArc");var subQ7=sQuery(id+"F0.wireOp",EDGE,"E1.top");var subQ8=sQuery(id+"F0.wireOp",EDGE,"E1.left");var subQ9=sQuery(id+"F0.wireOp",EDGE,"E1.right");var subQ10=sQuery(id+"F0.wireOp",EDGE,"E23.filletArc");var subQ11=sQuery(id+"F0.wireOp",EDGE,"E24.filletArc");Q0=makeQuery(id+"F2.boolean.opBoolean","SPLIT",FACE,{"disambiguationData":[TD([makeQuery(id+"F1.opExtrude","SWEPT_FACE",FACE,{"disambiguationData":[OSD([subQ5])]})])],"derivedFrom":makeQuery(id+"F1.opExtrude","CAP_FACE",FACE,{"disambiguationData":[OSD([subQ5,subQ7,subQ8,subQ9,subQ4,subQ3,subQ2,subQ1,subQ6,subQ0,subQ10,subQ11])],"isStart":true})});}
            var sketch = newSketch(context, id + "F16", { "sketchPlane" : qUnion([Q0])});
            skLineSegment(sketch, "E79", {"start": v(0, 74.25) * mm, "end": v(0, 104.25) * mm, "construction": true});
            skLineSegment(sketch, "E80", {"start": v(-33, 74.25) * mm, "end": v(-15, 92.25) * mm});
            skLineSegment(sketch, "E81", {"start": v(-15, 104.25) * mm, "end": v(-15, 92.25) * mm});
            skArc(sketch, "E82", {"start": v(15, 104.25) * mm, "mid": v(0, 119.25) * mm, "end": v(-15, 104.25) * mm});
            skLineSegment(sketch, "E83", {"start": v(15, 104.25) * mm, "end": v(15, 92.25) * mm});
            skLineSegment(sketch, "E84", {"start": v(15, 92.25) * mm, "end": v(33, 74.25) * mm});
            skCircle(sketch, "E85", {"center": v(0, 104.25) * mm, "radius": 6 * mm});
            skLineSegment(sketch, "E86", {"start": v(-33, 74.25) * mm, "end": v(33, 74.25) * mm});
            skLineSegment(sketch, "E87", {"start": v(-74.25, 0) * mm, "end": v(74.25, 0) * mm});
            skLineSegment(sketch, "E88.MirrorCS", {"start": v(-33, -74.25) * mm, "end": v(-15, -92.25) * mm});
            skLineSegment(sketch, "E89.MirrorCS", {"start": v(-15, -104.25) * mm, "end": v(-15, -92.25) * mm});
            skArc(sketch, "E90.MirrorCS", {"start": v(15, -104.25) * mm, "mid": v(0, -119.25) * mm, "end": v(-15, -104.25) * mm});
            skLineSegment(sketch, "E91.MirrorCS", {"start": v(15, -104.25) * mm, "end": v(15, -92.25) * mm});
            skLineSegment(sketch, "E92.MirrorCS", {"start": v(15, -92.25) * mm, "end": v(33, -74.25) * mm});
            skCircle(sketch, "E93.MirrorC", {"center": v(0, -104.25) * mm, "radius": 6 * mm});
            skLineSegment(sketch, "E94.MirrorCS", {"start": v(0, -74.25) * mm, "end": v(0, -104.25) * mm, "construction": true});
            skSolve(sketch);
        }
        {
            var Q0;
            {var subQ0=sQuery(id+"F16.wireOp",EDGE,"E88.MirrorCS");Q0=makeQuery(id+"F16.imprint","IMPRINT",FACE,{"disambiguationData":[TD([[makeQuery(id+"F16.imprint","IMPRINT",EDGE,{"derivedFrom":subQ0}),1.0]])]});}
            var Q1;
            Q1=makeQuery(id+"F16.imprint","IMPRINT",FACE,{"disambiguationData":[TD([[makeQuery(id+"F16.imprint","IMPRINT",EDGE,{"derivedFrom":sQuery(id+"F16.wireOp",EDGE,"E80")}),-1.0]])]});
            var Q2;
            Q2=makeQuery(id+"F2.opExtrude","CAP_FACE",FACE,{"disambiguationData":[OSD([sQuery(id+"F0.wireOp",EDGE,"E12"),sQuery(id+"F0.wireOp",EDGE,"E13"),sQuery(id+"F0.wireOp",EDGE,"E14"),sQuery(id+"F0.wireOp",EDGE,"E15"),sQuery(id+"F0.wireOp",EDGE,"E17.filletArc"),sQuery(id+"F0.wireOp",EDGE,"E18.filletArc"),sQuery(id+"F0.wireOp",EDGE,"E19.filletArc"),sQuery(id+"F0.wireOp",EDGE,"E20.filletArc"),sQuery(id+"F0.wireOp",EDGE,"E25.0"),sQuery(id+"F0.wireOp",EDGE,"E25.1"),sQuery(id+"F0.wireOp",EDGE,"E25.2"),sQuery(id+"F0.wireOp",EDGE,"E25.3"),sQuery(id+"F0.wireOp",EDGE,"E25.4"),sQuery(id+"F0.wireOp",EDGE,"E25.5"),sQuery(id+"F0.wireOp",EDGE,"E25.6"),sQuery(id+"F0.wireOp",EDGE,"E25.7")])],"isStart":false});
            extrude(context, id + "F17", {"entities" : qUnion([Q0, Q1]), "endBound" : BoundingType.UP_TO_SURFACE, "endBoundEntityFace" : qUnion([Q2]), "depth" : 25 * mm});
        }
        {
            var Q0;
            {var subQ0=sQuery(id+"F0.wireOp",EDGE,"E22.filletArc");var subQ1=sQuery(id+"F0.wireOp",EDGE,"E7");var subQ2=sQuery(id+"F0.wireOp",EDGE,"E6");var subQ3=sQuery(id+"F0.wireOp",EDGE,"E5");var subQ4=sQuery(id+"F0.wireOp",EDGE,"E4");var subQ5=sQuery(id+"F0.wireOp",EDGE,"E1.bottom");var subQ6=sQuery(id+"F0.wireOp",EDGE,"E21.filletArc");var subQ7=sQuery(id+"F0.wireOp",EDGE,"E1.top");var subQ8=sQuery(id+"F0.wireOp",EDGE,"E1.left");var subQ9=sQuery(id+"F0.wireOp",EDGE,"E1.right");var subQ10=sQuery(id+"F0.wireOp",EDGE,"E23.filletArc");var subQ11=sQuery(id+"F0.wireOp",EDGE,"E24.filletArc");Q0=makeQuery(id+"F2.boolean.opBoolean","SPLIT",FACE,{"disambiguationData":[TD([makeQuery(id+"F1.opExtrude","SWEPT_FACE",FACE,{"disambiguationData":[OSD([subQ5])]})])],"derivedFrom":makeQuery(id+"F1.opExtrude","CAP_FACE",FACE,{"disambiguationData":[OSD([subQ5,subQ7,subQ8,subQ9,subQ4,subQ3,subQ2,subQ1,subQ6,subQ0,subQ10,subQ11])],"isStart":true})});}
            var Q1;
            Q1=makeQuery(id+"F2.opExtrude","CAP_FACE",FACE,{"disambiguationData":[OSD([sQuery(id+"F0.wireOp",EDGE,"E12"),sQuery(id+"F0.wireOp",EDGE,"E13"),sQuery(id+"F0.wireOp",EDGE,"E14"),sQuery(id+"F0.wireOp",EDGE,"E15"),sQuery(id+"F0.wireOp",EDGE,"E17.filletArc"),sQuery(id+"F0.wireOp",EDGE,"E18.filletArc"),sQuery(id+"F0.wireOp",EDGE,"E19.filletArc"),sQuery(id+"F0.wireOp",EDGE,"E20.filletArc"),sQuery(id+"F0.wireOp",EDGE,"E25.0"),sQuery(id+"F0.wireOp",EDGE,"E25.1"),sQuery(id+"F0.wireOp",EDGE,"E25.2"),sQuery(id+"F0.wireOp",EDGE,"E25.3"),sQuery(id+"F0.wireOp",EDGE,"E25.4"),sQuery(id+"F0.wireOp",EDGE,"E25.5"),sQuery(id+"F0.wireOp",EDGE,"E25.6"),sQuery(id+"F0.wireOp",EDGE,"E25.7")])],"isStart":false});
            extrude(context, id + "F18", {"entities" : qUnion([Q0]), "endBound" : BoundingType.UP_TO_SURFACE, "endBoundEntityFace" : qUnion([Q1]), "depth" : 25 * mm});
        }
    });
